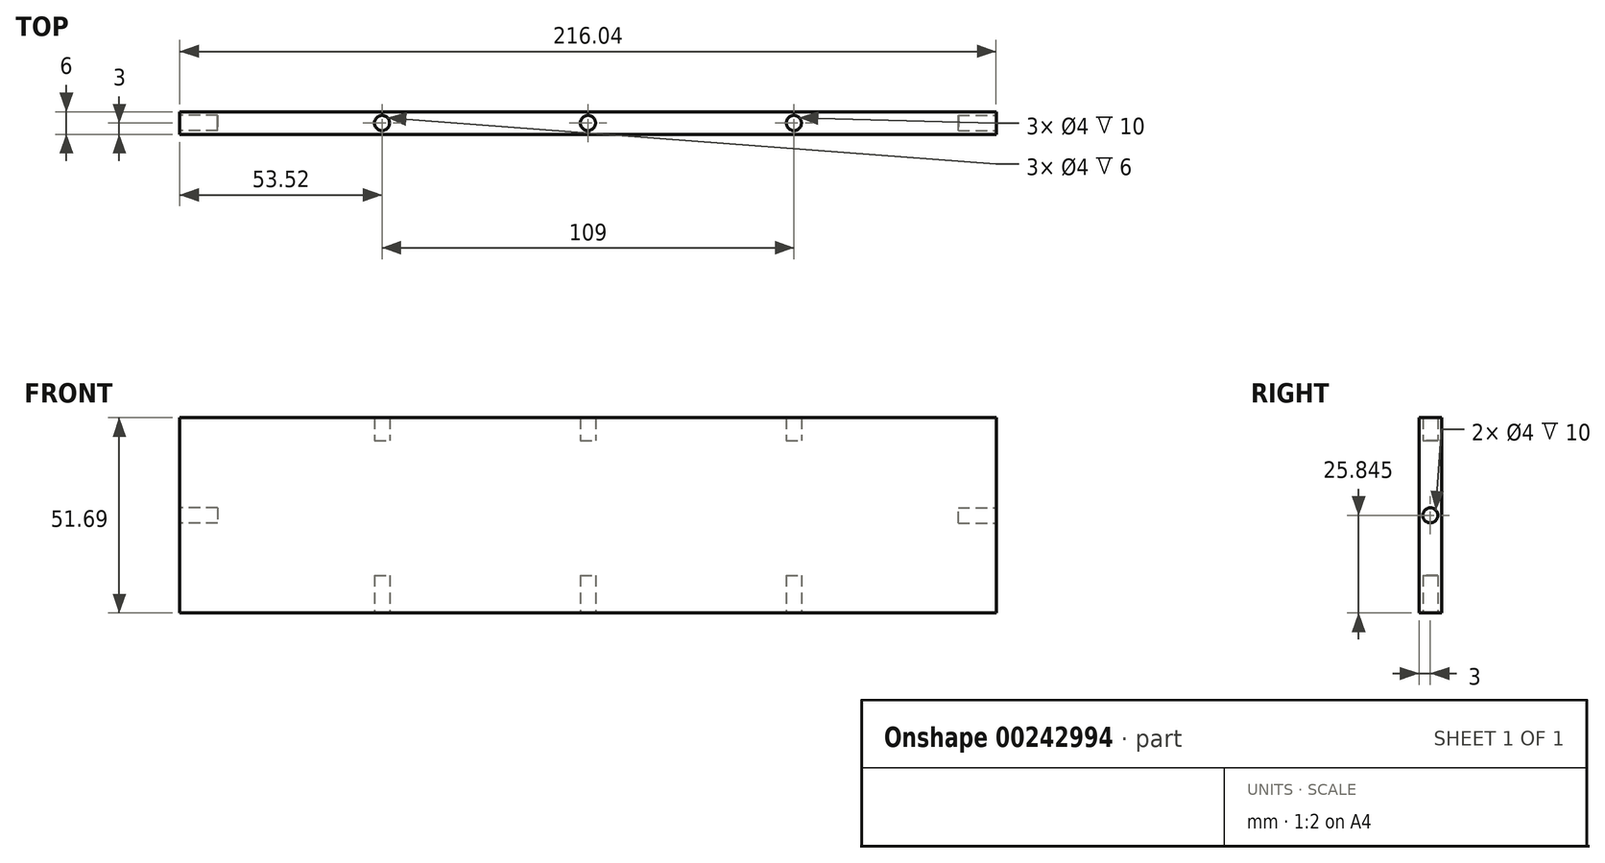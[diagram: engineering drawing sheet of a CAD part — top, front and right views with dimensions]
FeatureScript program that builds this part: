
annotation { "Feature Type Name" : "Feature", "Feature Type Description" : "" }
export const myFeature = defineFeature(function(context is Context, id is Id, definition is map)
    precondition{}
    {
        {
            var Q0;
            Q0=qCreatedBy(makeId("Front.planeOp"),FACE);
            var sketch = newSketch(context, id + "F0", { "sketchPlane" : qUnion([Q0])});
            skLineSegment(sketch, "E0.bottom", {"start": v(-108.02, 0) * mm, "end": v(108.02, 0) * mm});
            skLineSegment(sketch, "E0.top", {"start": v(-108.02, 51.7) * mm, "end": v(108.02, 51.7) * mm});
            skLineSegment(sketch, "E0.left", {"start": v(-108.02, 0) * mm, "end": v(-108.02, 51.7) * mm});
            skLineSegment(sketch, "E0.right", {"start": v(108.02, 0) * mm, "end": v(108.02, 51.7) * mm});
            skPoint(sketch, "E1", {"position": v(0, 0) * mm});
            skSolve(sketch);
        }
        {
            var Q0;
            Q0 = qSketchRegion(id + "F0", true);
            extrude(context, id + "F1", {"entities" : qUnion([Q0]), "depth" : 6 * mm});
        }
        {
            var Q0;
            Q0=makeQuery(id+"F1.opExtrude","SWEPT_FACE",FACE,{"disambiguationData":[OSD([sQuery(id+"F0.wireOp",EDGE,"E0.bottom")])]});
            var sketch = newSketch(context, id + "F2", { "sketchPlane" : qUnion([Q0])});
            skLineSegment(sketch, "E2", {"start": v(-112.02, 3) * mm, "end": v(150.1, 3) * mm, "construction": true});
            skCircle(sketch, "E3", {"center": v(0, 3) * mm, "radius": 2 * mm});
            skCircle(sketch, "E4", {"center": v(-54.5, 3) * mm, "radius": 2 * mm});
            skCircle(sketch, "E5", {"center": v(54.5, 3) * mm, "radius": 2 * mm});
            skSolve(sketch);
        }
        {
            var Q0;
            Q0 = qSketchRegion(id + "F2", true);
            extrude(context, id + "F3", {"entities" : qUnion([Q0]), "operationType" : NewBodyOperationType.REMOVE, "oppositeDirection" : true, "depth" : 10 * mm});
        }
        {
            var Q0;
            Q0=makeQuery(id+"F1.opExtrude","SWEPT_FACE",FACE,{"disambiguationData":[OSD([sQuery(id+"F0.wireOp",EDGE,"E0.left")])]});
            var sketch = newSketch(context, id + "F4", { "sketchPlane" : qUnion([Q0])});
            skLineSegment(sketch, "E6", {"start": v(3, 51.7) * mm, "end": v(3, 0) * mm, "construction": true});
            skLineSegment(sketch, "E7", {"start": v(3, 35.85) * mm, "end": v(3, 15.85) * mm});
            skPoint(sketch, "E8", {"position": v(3, 25.85) * mm});
            skCircle(sketch, "E9", {"center": v(3, 25.85) * mm, "radius": 2 * mm});
            skSolve(sketch);
        }
        {
            var Q0;
            Q0 = qSketchRegion(id + "F4", true);
            extrude(context, id + "F5", {"entities" : qUnion([Q0]), "operationType" : NewBodyOperationType.ADD, "oppositeDirection" : true, "depth" : 10 * mm});
        }
        {
            var Q0;
            Q0 = qSketchRegion(id + "F2", true);
            extrude(context, id + "F6", {"entities" : qUnion([Q0]), "operationType" : NewBodyOperationType.REMOVE, "oppositeDirection" : true, "depth" : 51.69 * mm, "hasSecondDirection" : true, "secondDirectionOppositeDirection" : true, "secondDirectionDepth" : (51.69 - 6) * mm});
        }
        {
            var Q0;
            {var subQ0=sQuery(id+"F4.wireOp",EDGE,"E9");var subQ1=sQuery(id+"F4.wireOp",EDGE,"E7");var subQ2=makeQuery(id+"F4.imprint","INTERSECT",VERTEX,{"disambiguationData":[OD(0.0)],"derivedFrom":[subQ1,subQ0]});Q0=makeQuery(id+"F4.imprint","IMPRINT",FACE,{"disambiguationData":[TD([[makeQuery(id+"F4.imprint","IMPRINT",EDGE,{"disambiguationData":[TD([[subQ2,1.0]])],"derivedFrom":subQ1}),-1.0]])]});}
            var Q1;
            {var subQ0=sQuery(id+"F4.wireOp",EDGE,"E9");var subQ1=sQuery(id+"F4.wireOp",EDGE,"E7");var subQ2=makeQuery(id+"F4.imprint","INTERSECT",VERTEX,{"disambiguationData":[OD(0.0)],"derivedFrom":[subQ1,subQ0]});Q1=makeQuery(id+"F4.imprint","IMPRINT",FACE,{"disambiguationData":[TD([[makeQuery(id+"F4.imprint","IMPRINT",EDGE,{"disambiguationData":[TD([[subQ2,1.0]])],"derivedFrom":subQ1}),1.0]])]});}
            extrude(context, id + "F7", {"entities" : qUnion([Q0, Q1]), "operationType" : NewBodyOperationType.REMOVE, "oppositeDirection" : true, "depth" : 10 * mm});
        }
        {
            var Q0;
            Q0=makeQuery(id+"F1.opExtrude","SWEPT_FACE",FACE,{"disambiguationData":[OSD([sQuery(id+"F0.wireOp",EDGE,"E0.right")])]});
            var sketch = newSketch(context, id + "F8", { "sketchPlane" : qUnion([Q0])});
            skLineSegment(sketch, "E10", {"start": v(-3, 51.7) * mm, "end": v(-3, 0) * mm, "construction": true});
            skCircle(sketch, "E11", {"center": v(-3, 25.84) * mm, "radius": 2 * mm});
            skSolve(sketch);
        }
        {
            var Q0;
            Q0 = qSketchRegion(id + "F8", true);
            extrude(context, id + "F9", {"entities" : qUnion([Q0]), "operationType" : NewBodyOperationType.REMOVE, "oppositeDirection" : true, "depth" : 10 * mm});
        }
    });
